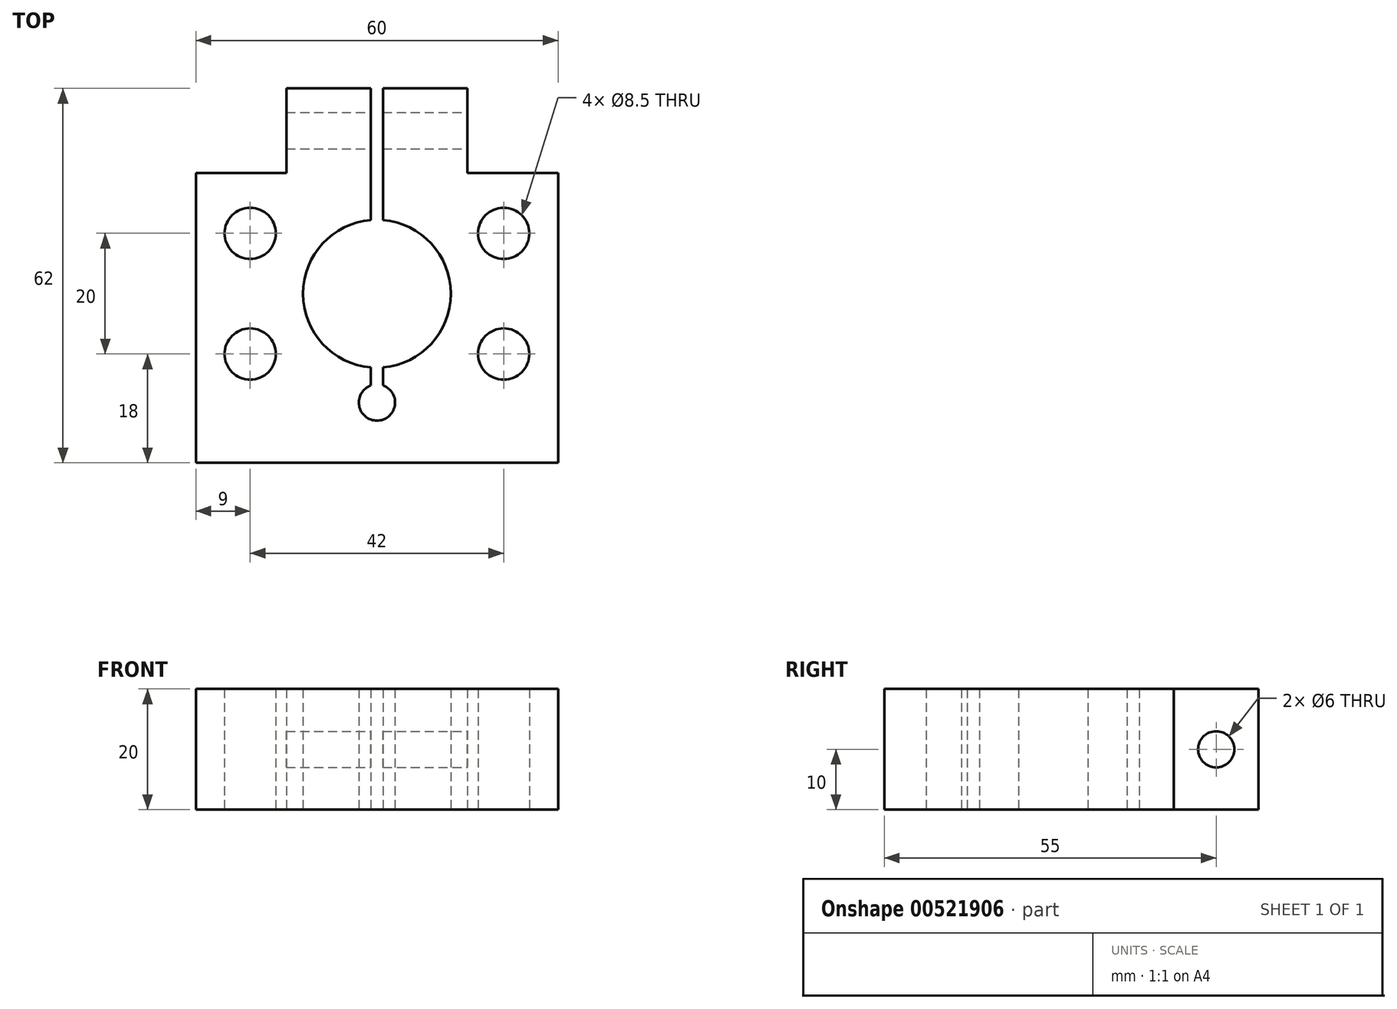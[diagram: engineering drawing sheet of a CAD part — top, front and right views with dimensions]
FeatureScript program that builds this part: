
annotation { "Feature Type Name" : "Feature", "Feature Type Description" : "" }
export const myFeature = defineFeature(function(context is Context, id is Id, definition is map)
    precondition{}
    {
        {
            var Q0;
            Q0=qCreatedBy(makeId("Top.planeOp"),FACE);
            var sketch = newSketch(context, id + "F0", { "sketchPlane" : qUnion([Q0])});
            skLineSegment(sketch, "E0.bottom", {"start": v(-15, 34) * mm, "end": v(-1, 34) * mm});
            skLineSegment(sketch, "E0.top", {"start": v(-30, -28) * mm, "end": v(30, -28) * mm});
            skLineSegment(sketch, "E0.left", {"start": v(-30, 20) * mm, "end": v(-30, -28) * mm});
            skLineSegment(sketch, "E0.right", {"start": v(30, 20) * mm, "end": v(30, -28) * mm});
            skArc(sketch, "E1", {"start": v(-1, 12.2) * mm, "mid": v(-12.25, 0) * mm, "end": v(-1, -12.2) * mm});
            skArc(sketch, "E2", {"start": v(-1, -15.2) * mm, "mid": v(0, -21.04) * mm, "end": v(1, -15.2) * mm});
            skLineSegment(sketch, "E3", {"start": v(-1, 34) * mm, "end": v(-1, 12.2) * mm});
            skLineSegment(sketch, "E4", {"start": v(1, 34) * mm, "end": v(1, 12.2) * mm});
            skLineSegment(sketch, "E5", {"start": v(0, 12.25) * mm, "end": v(0, 0) * mm, "construction": true});
            skLineSegment(sketch, "E6.trimOffspring", {"start": v(1, 34) * mm, "end": v(15, 34) * mm});
            skLineSegment(sketch, "E7", {"start": v(1, -15.2) * mm, "end": v(1, -12.2) * mm});
            skLineSegment(sketch, "E8", {"start": v(-1, -15.2) * mm, "end": v(-1, -12.2) * mm});
            skArc(sketch, "E9.trimOffspring", {"start": v(1, -12.2) * mm, "mid": v(12.25, 0) * mm, "end": v(1, 12.2) * mm});
            skCircle(sketch, "E10", {"center": v(-21, -10) * mm, "radius": 4.25 * mm});
            skCircle(sketch, "E11", {"center": v(21, -10) * mm, "radius": 4.25 * mm});
            skCircle(sketch, "E12", {"center": v(-21, 10) * mm, "radius": 4.25 * mm});
            skLineSegment(sketch, "E13", {"start": v(-30, 20) * mm, "end": v(-15, 20) * mm});
            skLineSegment(sketch, "E14", {"start": v(-15, 20) * mm, "end": v(-15, 34) * mm});
            skLineSegment(sketch, "E15", {"start": v(15, 34) * mm, "end": v(15, 20) * mm});
            skLineSegment(sketch, "E16", {"start": v(15, 20) * mm, "end": v(30, 20) * mm});
            skCircle(sketch, "E17", {"center": v(21, 10) * mm, "radius": 4.25 * mm});
            skSolve(sketch);
        }
        {
            var Q0;
            Q0=qSketchRegion(id+"F0",true);
            extrude(context, id + "F1", {"entities" : qUnion([Q0]), "depth" : 20 * mm, "offsetDistance" : 25 * mm});
        }
        {
            var Q0;
            Q0=makeQuery(id+"F1.opExtrude","SWEPT_FACE",FACE,{"disambiguationData":[OSD([sQuery(id+"F0.wireOp",EDGE,"E15")])]});
            var sketch = newSketch(context, id + "F2", { "sketchPlane" : qUnion([Q0])});
            skCircle(sketch, "E18", {"center": v(27, 10) * mm, "radius": 3 * mm});
            skPoint(sketch, "E18.centerSnap0", {"position": v(27, 20) * mm});
            skPoint(sketch, "E18.centerSnap1", {"position": v(20, 10) * mm});
            skSolve(sketch);
        }
        {
            var Q0;
            Q0=qSketchRegion(id+"F2",true);
            extrude(context, id + "F3", {"entities" : qUnion([Q0]), "operationType" : NewBodyOperationType.REMOVE, "oppositeDirection" : true, "depth" : 30 * mm, "offsetDistance" : 25 * mm});
        }
    });
